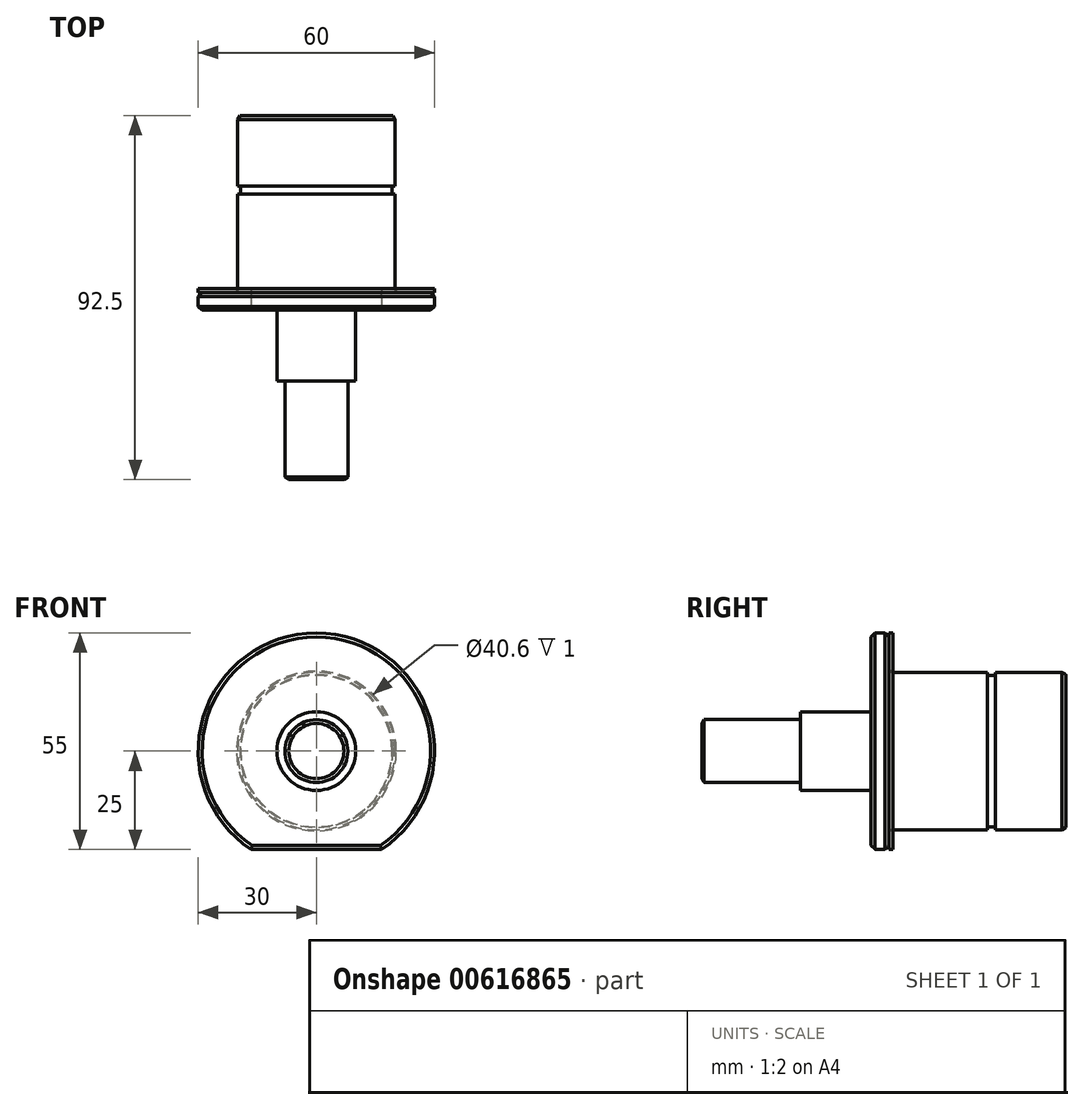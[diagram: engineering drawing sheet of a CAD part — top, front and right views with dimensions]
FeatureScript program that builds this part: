
annotation { "Feature Type Name" : "Feature", "Feature Type Description" : "" }
export const myFeature = defineFeature(function(context is Context, id is Id, definition is map)
    precondition{}
    {
        {
            var Q0;
            Q0=qCreatedBy(makeId("Right.planeOp"),FACE);
            var sketch = newSketch(context, id + "F0", { "sketchPlane" : qUnion([Q0])});
            skLineSegment(sketch, "E0", {"start": v(0, 0) * mm, "end": v(0, -8) * mm});
            skLineSegment(sketch, "E1", {"start": v(0, -8) * mm, "end": v(25, -8) * mm});
            skLineSegment(sketch, "E2", {"start": v(25, -8) * mm, "end": v(25, -10) * mm});
            skLineSegment(sketch, "E3", {"start": v(25, -10) * mm, "end": v(43, -10) * mm});
            skLineSegment(sketch, "E4", {"start": v(43, -10) * mm, "end": v(43, -30) * mm});
            skLineSegment(sketch, "E5", {"start": v(43, -30) * mm, "end": v(47.5, -30) * mm});
            skLineSegment(sketch, "E6", {"start": v(47.5, -30) * mm, "end": v(47.5, -20) * mm});
            skLineSegment(sketch, "E7", {"start": v(47.5, -20) * mm, "end": v(92.5, -20) * mm});
            skLineSegment(sketch, "E8", {"start": v(92.5, -20) * mm, "end": v(92.5, 0) * mm});
            skLineSegment(sketch, "E9", {"start": v(92.5, 0) * mm, "end": v(0, 0) * mm});
            skLineSegment(sketch, "E10", {"start": v(-68.98, 0) * mm, "end": v(144.58, 0) * mm, "construction": true});
            skSolve(sketch);
        }
        {
            var Q0;
            Q0=makeQuery(id+"F0.imprint","IMPRINT",FACE,{"disambiguationData":[TD([[makeQuery(id+"F0.imprint","IMPRINT",EDGE,{"derivedFrom":sQuery(id+"F0.wireOp",EDGE,"E0")}),1.0]])]});
            var Q1;
            Q1=sQuery(id+"F0.wireOp",EDGE,"E10");
            revolve(context, id + "F1", {"surfaceOperationType" : NewSurfaceOperationType.NEW, "entities" : qUnion([Q0]), "axis" : qUnion([Q1]), "revolveType" : RevolveType.FULL});
        }
        {
            var Q0;
            Q0=qCreatedBy(makeId("Front.planeOp"),FACE);
            var sketch = newSketch(context, id + "F2", { "sketchPlane" : qUnion([Q0])});
            skLineSegment(sketch, "E11.bottom", {"start": v(30, -25) * mm, "end": v(-30, -25) * mm});
            skLineSegment(sketch, "E11.top", {"start": v(30, -35) * mm, "end": v(-30, -35) * mm});
            skLineSegment(sketch, "E11.left", {"start": v(30, -25) * mm, "end": v(30, -35) * mm});
            skLineSegment(sketch, "E11.right", {"start": v(-30, -25) * mm, "end": v(-30, -35) * mm});
            skSolve(sketch);
        }
        {
            var Q0;
            Q0 = qSketchRegion(id + "F2", true);
            extrude(context, id + "F3", {"entities" : qUnion([Q0]), "operationType" : NewBodyOperationType.REMOVE, "endBound" : BoundingType.THROUGH_ALL, "oppositeDirection" : true, "depth" : 25 * mm, "offsetDistance" : 25 * mm});
        }
        {
            var Q0;
            Q0=makeQuery(id+"F1.opRevolve","SWEPT_EDGE",EDGE,{"disambiguationData":[OSD([sQuery(id+"F0.wireOp",EDGE,"E5"),sQuery(id+"F0.wireOp",EDGE,"E6")])]});
            var Q1;
            Q1=makeQuery(id+"F3.boolean.opBoolean","INTERSECT",EDGE,{"derivedFrom":[makeQuery(id+"F1.opRevolve","SWEPT_FACE",FACE,{"disambiguationData":[OSD([sQuery(id+"F0.wireOp",EDGE,"E6")])]}),makeQuery(id+"F3.opExtrude","SWEPT_FACE",FACE,{"disambiguationData":[OSD([sQuery(id+"F2.wireOp",EDGE,"E11.bottom")])]})]});
            var Q2;
            Q2=makeQuery(id+"F1.opRevolve","SWEPT_EDGE",EDGE,{"disambiguationData":[OSD([sQuery(id+"F0.wireOp",EDGE,"E4"),sQuery(id+"F0.wireOp",EDGE,"E5")])]});
            var Q3;
            Q3=makeQuery(id+"F3.boolean.opBoolean","INTERSECT",EDGE,{"derivedFrom":[makeQuery(id+"F1.opRevolve","SWEPT_FACE",FACE,{"disambiguationData":[OSD([sQuery(id+"F0.wireOp",EDGE,"E4")])]}),makeQuery(id+"F3.opExtrude","SWEPT_FACE",FACE,{"disambiguationData":[OSD([sQuery(id+"F2.wireOp",EDGE,"E11.bottom")])]})]});
            chamfer(context, id + "F4", {"entities" : qUnion([Q0, Q1, Q2, Q3]), "width" : 1 * mm, "tangentPropagation" : true});
        }
        {
            var Q0;
            Q0=makeQuery(id+"F1.opRevolve","SWEPT_EDGE",EDGE,{"disambiguationData":[OSD([sQuery(id+"F0.wireOp",EDGE,"E0"),sQuery(id+"F0.wireOp",EDGE,"E1")])]});
            var Q1;
            Q1=makeQuery(id+"F1.opRevolve","SWEPT_EDGE",EDGE,{"disambiguationData":[OSD([sQuery(id+"F0.wireOp",EDGE,"E7"),sQuery(id+"F0.wireOp",EDGE,"E8")])]});
            chamfer(context, id + "F5", {"entities" : qUnion([Q0, Q1]), "chamferType" : ChamferType.OFFSET_ANGLE, "width" : 1 * mm, "oppositeDirection" : false, "angle" : 30 * degree, "tangentPropagation" : true});
        }
        {
            var Q0;
            Q0=qCreatedBy(makeId("Right.planeOp"),FACE);
            var sketch = newSketch(context, id + "F6", { "sketchPlane" : qUnion([Q0])});
            skLineSegment(sketch, "E12", {"start": v(72.5, 19.25) * mm, "end": v(72.5, 21.25) * mm});
            skLineSegment(sketch, "E13", {"start": v(72.5, 21.25) * mm, "end": v(74.5, 21.25) * mm});
            skLineSegment(sketch, "E14", {"start": v(74.5, 21.25) * mm, "end": v(74.5, 19.25) * mm});
            skLineSegment(sketch, "E15", {"start": v(47.5, 20) * mm, "end": v(91.5, 20) * mm, "construction": true});
            skLineSegment(sketch, "E16", {"start": v(72.5, 19.25) * mm, "end": v(74.5, 19.25) * mm});
            skLineSegment(sketch, "E17", {"start": v(77.36, 0) * mm, "end": v(55.72, 0) * mm, "construction": true});
            skSolve(sketch);
        }
        {
            var Q0;
            Q0=makeQuery(id+"F6.imprint","IMPRINT",FACE,{"disambiguationData":[TD([[makeQuery(id+"F6.imprint","IMPRINT",EDGE,{"derivedFrom":sQuery(id+"F6.wireOp",EDGE,"E12")}),-1.0]])]});
            var Q1;
            Q1=sQuery(id+"F6.wireOp",EDGE,"E17");
            revolve(context, id + "F7", {"operationType" : NewBodyOperationType.REMOVE, "surfaceOperationType" : NewSurfaceOperationType.NEW, "entities" : qUnion([Q0]), "axis" : qUnion([Q1]), "revolveType" : RevolveType.FULL, "oppositeDirection" : true});
        }
        {
            var Q0;
            Q0=makeQuery(id+"F1.opRevolve","SWEPT_FACE",FACE,{"disambiguationData":[OSD([sQuery(id+"F0.wireOp",EDGE,"E6")])]});
            var sketch = newSketch(context, id + "F8", { "sketchPlane" : qUnion([Q0])});
            skArc(sketch, "E18.0", {"start": v(-16.58, -25) * mm, "mid": v(0, 30) * mm, "end": v(16.58, -25) * mm});
            skLineSegment(sketch, "E19.0", {"start": v(16.58, -25) * mm, "end": v(-16.58, -25) * mm});
            skCircle(sketch, "E20.0", {"center": v(0, 0) * mm, "radius": 20 * mm, "construction": true});
            skCircle(sketch, "E21.0", {"center": v(0, 0) * mm, "radius": 20.3 * mm});
            skSolve(sketch);
        }
        {
            var Q0;
            Q0 = qSketchRegion(id + "F8", true);
            extrude(context, id + "F9", {"entities" : qUnion([Q0]), "depth" : 1 * mm, "offsetDistance" : 25 * mm});
        }
    });
